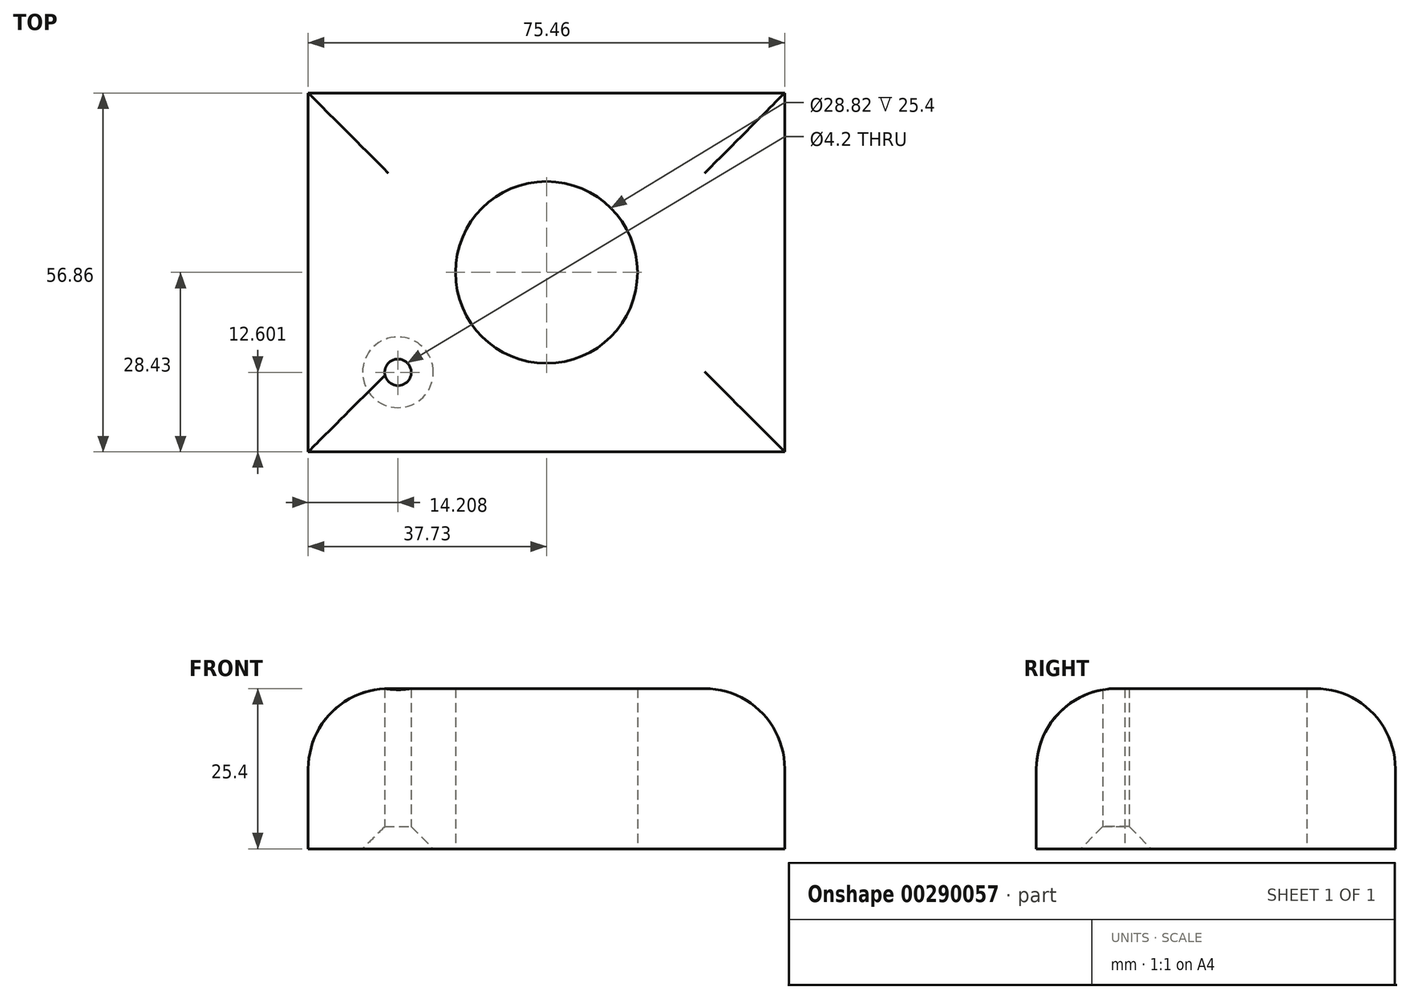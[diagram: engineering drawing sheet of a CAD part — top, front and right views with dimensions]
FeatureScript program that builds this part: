
annotation { "Feature Type Name" : "Feature", "Feature Type Description" : "" }
export const myFeature = defineFeature(function(context is Context, id is Id, definition is map)
    precondition{}
    {
        {
            var Q0;
            Q0=qCreatedBy(makeId("Top.planeOp"),FACE);
            var sketch = newSketch(context, id + "F0", { "sketchPlane" : qUnion([Q0])});
            skLineSegment(sketch, "E0.bottom", {"start": v(37.73, 28.43) * mm, "end": v(-37.73, 28.43) * mm});
            skLineSegment(sketch, "E0.top", {"start": v(37.73, -28.43) * mm, "end": v(-37.73, -28.43) * mm});
            skLineSegment(sketch, "E0.left", {"start": v(37.73, 28.43) * mm, "end": v(37.73, -28.43) * mm});
            skLineSegment(sketch, "E0.right", {"start": v(-37.73, 28.43) * mm, "end": v(-37.73, -28.43) * mm});
            skPoint(sketch, "E0.middle", {"position": v(0, 0) * mm});
            skCircle(sketch, "E1", {"center": v(0, 0) * mm, "radius": 14.41 * mm});
            skLineSegment(sketch, "E2", {"start": v(-37.73, 28.43) * mm, "end": v(0, 0) * mm});
            skSolve(sketch);
        }
        {
            var Q0;
            Q0=makeQuery(id+"F0.imprint","IMPRINT",FACE,{"disambiguationData":[TD([[makeQuery(id+"F0.imprint","IMPRINT",EDGE,{"derivedFrom":sQuery(id+"F0.wireOp",EDGE,"E0.bottom")}),1.0]])]});
            extrude(context, id + "F1", {"entities" : qUnion([Q0]), "depth" : 25.4 * mm});
        }
        {
            var Q0;
            Q0=makeQuery(id+"F1.opExtrude","CAP_EDGE",EDGE,{"disambiguationData":[OSD([sQuery(id+"F0.wireOp",EDGE,"E0.top")])],"isStart":false});
            var Q1;
            Q1=makeQuery(id+"F1.opExtrude","CAP_EDGE",EDGE,{"disambiguationData":[OSD([sQuery(id+"F0.wireOp",EDGE,"E0.right")])],"isStart":false});
            var Q2;
            Q2=makeQuery(id+"F1.opExtrude","CAP_EDGE",EDGE,{"disambiguationData":[OSD([sQuery(id+"F0.wireOp",EDGE,"E0.bottom")])],"isStart":false});
            var Q3;
            Q3=makeQuery(id+"F1.opExtrude","CAP_EDGE",EDGE,{"disambiguationData":[OSD([sQuery(id+"F0.wireOp",EDGE,"E0.left")])],"isStart":false});
            fillet(context, id + "F2", {"entities" : qUnion([Q0, Q1, Q2, Q3]), "radius" : 12.7 * mm, "tangentPropagation" : true, "allowEdgeOverflow" : false});
        }
        {
            var Q0;
            Q0=makeQuery(id+"F1.opExtrude","CAP_FACE",FACE,{"disambiguationData":[OSD([sQuery(id+"F0.wireOp",EDGE,"E0.bottom"),sQuery(id+"F0.wireOp",EDGE,"E0.top"),sQuery(id+"F0.wireOp",EDGE,"E0.left"),sQuery(id+"F0.wireOp",EDGE,"E0.right"),sQuery(id+"F0.wireOp",EDGE,"E1")])],"isStart":true});
            var sketch = newSketch(context, id + "F3", { "sketchPlane" : qUnion([Q0])});
            skPoint(sketch, "E3", {"position": v(-23.52, 15.83) * mm});
            skSolve(sketch);
        }
        {
            var Q0;
            Q0=sQuery(id+"F3.wireOp",VERTEX,"E3");
            var Q1;
            Q1=makeQuery(id+"F1.opExtrude","SWEPT_BODY",BODY,{"disambiguationData":[OSD([sQuery(id+"F0.wireOp",EDGE,"E0.bottom"),sQuery(id+"F0.wireOp",EDGE,"E0.top"),sQuery(id+"F0.wireOp",EDGE,"E0.left"),sQuery(id+"F0.wireOp",EDGE,"E0.right"),sQuery(id+"F0.wireOp",EDGE,"E1")])]});
            hole(context, id + "F4", {"style" : HoleStyle.C_SINK, "endStyle" : HoleEndStyle.THROUGH, "standardTappedOrClearance" : lookupTablePath({ "standard" : "ISO", "engagement" : "75%", "pitch" : "0.8 mm", "size" : "M5", "type" : "Tapped" }), "standardBlindInLast" : lookupTablePath({ "standard" : "ISO", "engagement" : "75%", "pitch" : "0.8 mm", "size" : "M5", "type" : "Tapped" }), "holeDiameter" : 4.2 * mm, "cSinkDiameter" : 11.2 * mm, "cSinkAngle" : 90 * degree, "showTappedDepth" : true, "tappedDepth" : 12.7 * mm, "tapClearance" : 3, "locations" : qUnion([Q0]), "scope" : qUnion([Q1]), "majorDiameter" : 5 * mm});
        }
    });
